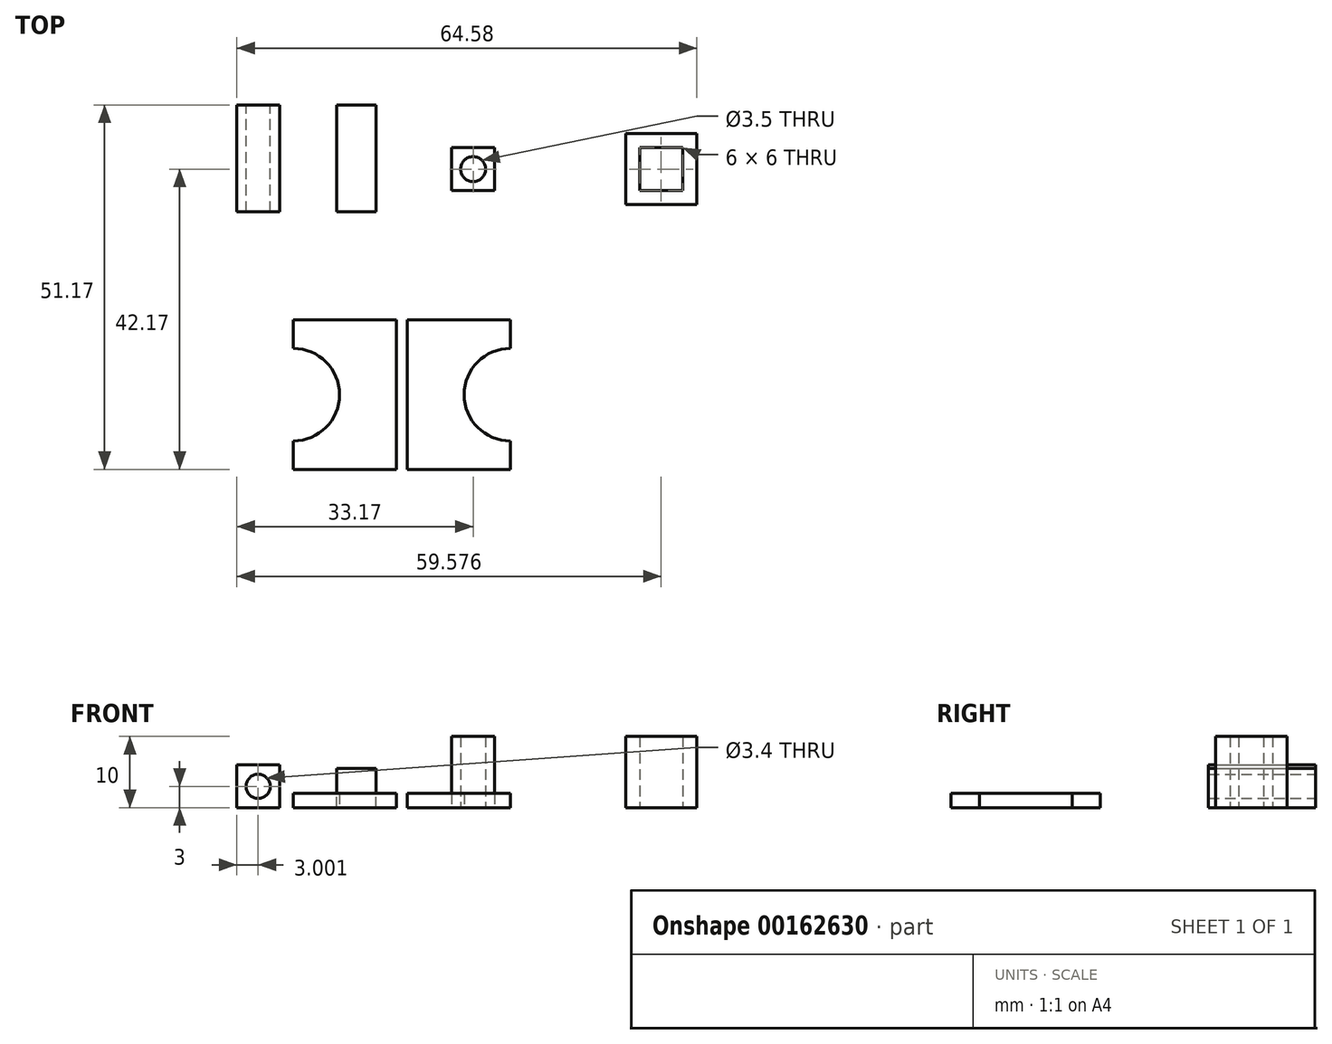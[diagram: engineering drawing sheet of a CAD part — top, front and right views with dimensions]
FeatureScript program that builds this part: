
annotation { "Feature Type Name" : "Feature", "Feature Type Description" : "" }
export const myFeature = defineFeature(function(context is Context, id is Id, definition is map)
    precondition{}
    {
        {
            var Q0;
            Q0=qCreatedBy(makeId("Front.planeOp"),FACE);
            var sketch = newSketch(context, id + "F0", { "sketchPlane" : qUnion([Q0])});
            skLineSegment(sketch, "E0.bottom", {"start": v(-23.17, 0) * mm, "end": v(-17.17, 0) * mm});
            skLineSegment(sketch, "E0.top", {"start": v(-23.17, 6) * mm, "end": v(-17.17, 6) * mm});
            skLineSegment(sketch, "E0.left", {"start": v(-23.17, 0) * mm, "end": v(-23.17, 6) * mm});
            skLineSegment(sketch, "E0.right", {"start": v(-17.17, 0) * mm, "end": v(-17.17, 6) * mm});
            skCircle(sketch, "E1", {"center": v(-20.17, 3) * mm, "radius": 1.7 * mm});
            skPoint(sketch, "E1.centerSnap0", {"position": v(-23.17, 3) * mm});
            skPoint(sketch, "E1.centerSnap1", {"position": v(-20.17, 6) * mm});
            skLineSegment(sketch, "E2.bottom", {"start": v(-9.15, 0) * mm, "end": v(-3.65, 0) * mm});
            skLineSegment(sketch, "E2.top", {"start": v(-9.15, 5.5) * mm, "end": v(-3.65, 5.5) * mm});
            skLineSegment(sketch, "E2.left", {"start": v(-9.15, 0) * mm, "end": v(-9.15, 5.5) * mm});
            skLineSegment(sketch, "E2.right", {"start": v(-3.65, 0) * mm, "end": v(-3.65, 5.5) * mm});
            skSolve(sketch);
        }
        {
            var Q0;
            Q0=qCreatedBy(makeId("Top.planeOp"),FACE);
            var sketch = newSketch(context, id + "F1", { "sketchPlane" : qUnion([Q0])});
            skLineSegment(sketch, "E3.bottom", {"start": v(3, 3) * mm, "end": v(-3, 3) * mm});
            skLineSegment(sketch, "E3.top", {"start": v(3, -3) * mm, "end": v(-3, -3) * mm});
            skLineSegment(sketch, "E3.left", {"start": v(3, 3) * mm, "end": v(3, -3) * mm});
            skLineSegment(sketch, "E3.right", {"start": v(-3, 3) * mm, "end": v(-3, -3) * mm});
            skPoint(sketch, "E3.middle", {"position": v(0, 0) * mm});
            skCircle(sketch, "E4", {"center": v(0, 0) * mm, "radius": 1.75 * mm});
            skLineSegment(sketch, "E5.bottom", {"start": v(29.4, 3) * mm, "end": v(23.4, 3) * mm});
            skLineSegment(sketch, "E5.top", {"start": v(29.4, -3) * mm, "end": v(23.4, -3) * mm});
            skLineSegment(sketch, "E5.left", {"start": v(29.4, 3) * mm, "end": v(29.4, -3) * mm});
            skLineSegment(sketch, "E5.right", {"start": v(23.4, 3) * mm, "end": v(23.4, -3) * mm});
            skPoint(sketch, "E5.middle", {"position": v(26.4, 0) * mm});
            skLineSegment(sketch, "E6.bottom", {"start": v(31.4, 5) * mm, "end": v(21.4, 5) * mm});
            skLineSegment(sketch, "E6.top", {"start": v(31.4, -5) * mm, "end": v(21.4, -5) * mm});
            skLineSegment(sketch, "E6.left", {"start": v(31.4, 5) * mm, "end": v(31.4, -5) * mm});
            skLineSegment(sketch, "E6.right", {"start": v(21.4, 5) * mm, "end": v(21.4, -5) * mm});
            skLineSegment(sketch, "E7", {"start": v(-0.75, -30.17) * mm, "end": v(-15.25, -30.17) * mm});
            skLineSegment(sketch, "E8", {"start": v(-0.75, -30.17) * mm, "end": v(-0.75, -51.17) * mm});
            skLineSegment(sketch, "E9", {"start": v(-0.75, -51.17) * mm, "end": v(-15.25, -51.17) * mm});
            skLineSegment(sketch, "E10", {"start": v(-15.25, -30.17) * mm, "end": v(-15.25, -34.17) * mm});
            skLineSegment(sketch, "E11", {"start": v(-15.25, -51.17) * mm, "end": v(-15.25, -47.17) * mm});
            skArc(sketch, "E12", {"start": v(-15.25, -47.17) * mm, "mid": v(-8.75, -40.67) * mm, "end": v(-15.25, -34.17) * mm});
            skLineSegment(sketch, "E13.MirrorCS", {"start": v(0.75, -51.17) * mm, "end": v(15.25, -51.17) * mm});
            skLineSegment(sketch, "E14.MirrorCS", {"start": v(0.75, -30.17) * mm, "end": v(0.75, -51.17) * mm});
            skLineSegment(sketch, "E15.MirrorCS", {"start": v(0.75, -30.17) * mm, "end": v(15.25, -30.17) * mm});
            skLineSegment(sketch, "E16.MirrorCS", {"start": v(15.25, -30.17) * mm, "end": v(15.25, -34.17) * mm});
            skArc(sketch, "E17.MirrorCS", {"start": v(15.25, -47.17) * mm, "mid": v(8.75, -40.67) * mm, "end": v(15.25, -34.17) * mm});
            skLineSegment(sketch, "E18.MirrorCS", {"start": v(15.25, -51.17) * mm, "end": v(15.25, -47.17) * mm});
            skSolve(sketch);
        }
        {
            var Q0;
            Q0=makeQuery(id+"F0.imprint","IMPRINT",FACE,{"disambiguationData":[TD([[makeQuery(id+"F0.imprint","IMPRINT",EDGE,{"derivedFrom":sQuery(id+"F0.wireOp",EDGE,"E0.bottom")}),1.0]])]});
            var Q1;
            Q1=makeQuery(id+"F0.imprint","IMPRINT",FACE,{"disambiguationData":[TD([[makeQuery(id+"F0.imprint","IMPRINT",EDGE,{"derivedFrom":sQuery(id+"F0.wireOp",EDGE,"E2.bottom")}),1.0]])]});
            extrude(context, id + "F2", {"entities" : qUnion([Q0, Q1]), "depth" : 15 * mm});
        }
        {
            var Q0;
            Q0=makeQuery(id+"F1.imprint","IMPRINT",FACE,{"disambiguationData":[TD([[makeQuery(id+"F1.imprint","IMPRINT",EDGE,{"derivedFrom":sQuery(id+"F1.wireOp",EDGE,"E3.bottom")}),1.0]])]});
            var Q1;
            Q1=makeQuery(id+"F1.imprint","IMPRINT",FACE,{"disambiguationData":[TD([[makeQuery(id+"F1.imprint","IMPRINT",EDGE,{"derivedFrom":sQuery(id+"F1.wireOp",EDGE,"E5.bottom")}),-1.0]])]});
            extrude(context, id + "F3", {"entities" : qUnion([Q0, Q1]), "depth" : 10 * mm});
        }
        {
            var Q0;
            Q0=makeQuery(id+"F3.opExtrude","SWEPT_BODY",BODY,{"disambiguationData":[OSD([sQuery(id+"F1.wireOp",EDGE,"E3.bottom"),sQuery(id+"F1.wireOp",EDGE,"E3.top"),sQuery(id+"F1.wireOp",EDGE,"E3.left"),sQuery(id+"F1.wireOp",EDGE,"E3.right"),sQuery(id+"F1.wireOp",EDGE,"E4")])]});
            var Q1;
            Q1=makeQuery(id+"F3.opExtrude","SWEPT_BODY",BODY,{"disambiguationData":[OSD([sQuery(id+"F1.wireOp",EDGE,"E5.bottom"),sQuery(id+"F1.wireOp",EDGE,"E5.top"),sQuery(id+"F1.wireOp",EDGE,"E5.left"),sQuery(id+"F1.wireOp",EDGE,"E5.right"),sQuery(id+"F1.wireOp",EDGE,"E6.bottom"),sQuery(id+"F1.wireOp",EDGE,"E6.top"),sQuery(id+"F1.wireOp",EDGE,"E6.left"),sQuery(id+"F1.wireOp",EDGE,"E6.right")])]});
            transform(context, id + "F4", {"entities" : qUnion([Q0, Q1]), "transformType" : TransformType.TRANSLATION_3D, "dx" : 10 * mm, "dy" : -9 * mm, "dz" : 0 * mm, "makeCopy" : false});
        }
        {
            var Q0;
            Q0=makeQuery(id+"F1.imprint","IMPRINT",FACE,{"disambiguationData":[TD([[makeQuery(id+"F1.imprint","IMPRINT",EDGE,{"derivedFrom":sQuery(id+"F1.wireOp",EDGE,"E7")}),1.0]])]});
            var Q1;
            Q1=makeQuery(id+"F1.imprint","IMPRINT",FACE,{"disambiguationData":[TD([[makeQuery(id+"F1.imprint","IMPRINT",EDGE,{"derivedFrom":sQuery(id+"F1.wireOp",EDGE,"E13.MirrorCS")}),1.0]])]});
            extrude(context, id + "F5", {"entities" : qUnion([Q0, Q1]), "depth" : 2 * mm});
        }
    });
